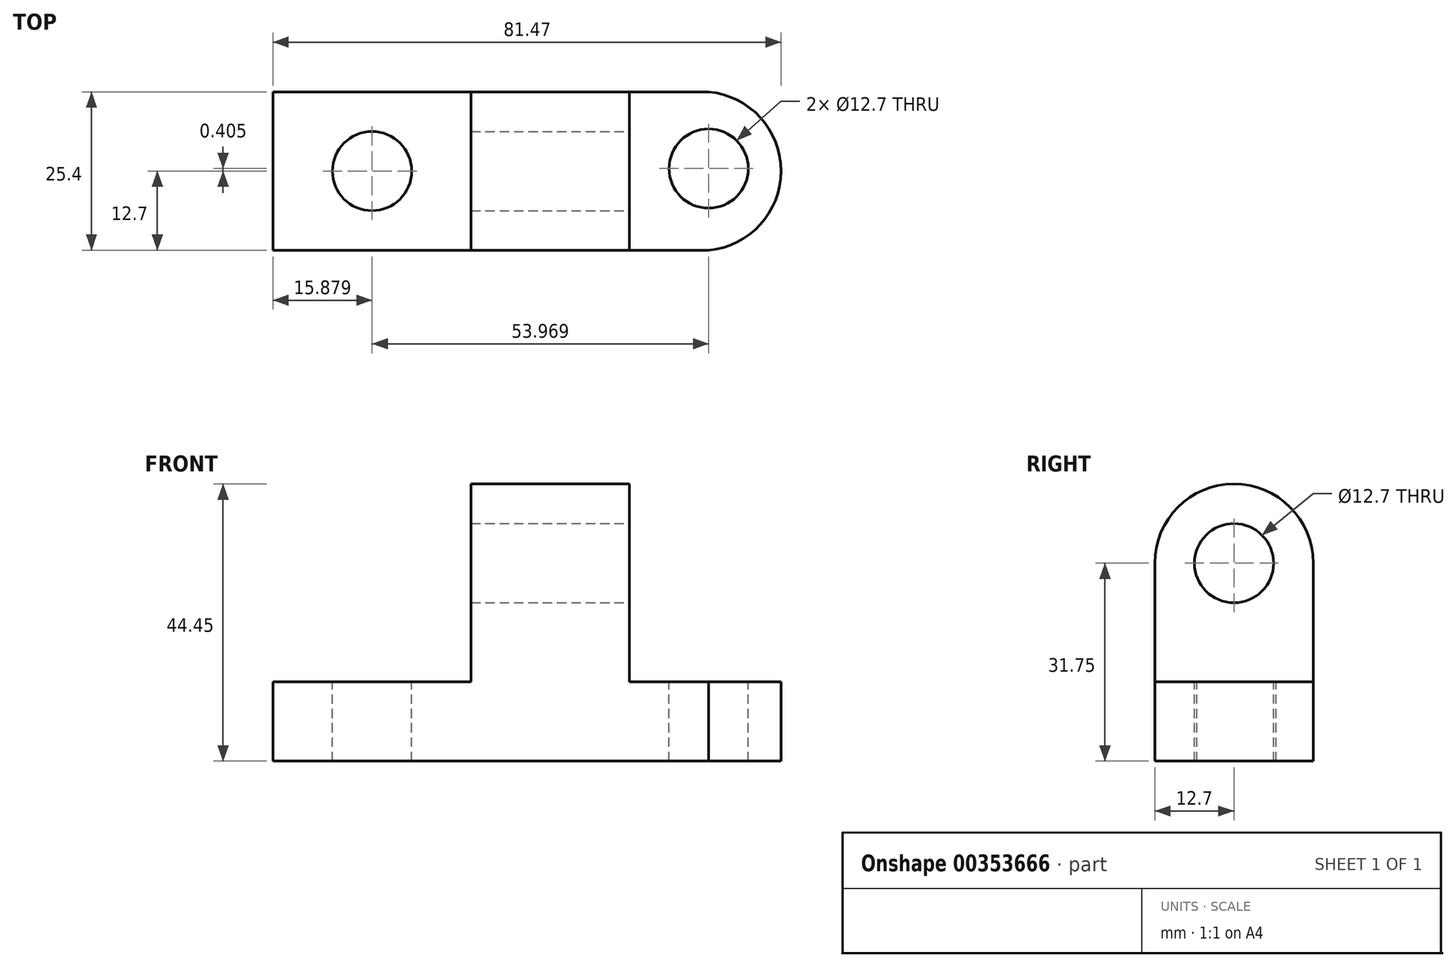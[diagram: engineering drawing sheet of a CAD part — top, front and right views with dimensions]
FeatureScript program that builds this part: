
annotation { "Feature Type Name" : "Feature", "Feature Type Description" : "" }
export const myFeature = defineFeature(function(context is Context, id is Id, definition is map)
    precondition{}
    {
        {
            var Q0;
            Q0=qCreatedBy(makeId("Front.planeOp"),FACE);
            var sketch = newSketch(context, id + "F0", { "sketchPlane" : qUnion([Q0])});
            skLineSegment(sketch, "E0", {"start": v(-42.78, 63.5) * mm, "end": v(-42.78, 0) * mm});
            skLineSegment(sketch, "E1", {"start": v(-42.78, 0) * mm, "end": v(46.12, 0) * mm});
            skLineSegment(sketch, "E2", {"start": v(46.12, 0) * mm, "end": v(46.12, 63.5) * mm});
            skLineSegment(sketch, "E3", {"start": v(46.12, 63.5) * mm, "end": v(-42.78, 63.5) * mm});
            skSolve(sketch);
        }
        {
            var Q0;
            Q0 = qSketchRegion(id + "F0", true);
            extrude(context, id + "F1", {"entities" : qUnion([Q0]), "depth" : 25.4 * mm});
        }
        {
            var Q0;
            Q0=makeQuery(id+"F1.opExtrude","CAP_FACE",FACE,{"disambiguationData":[OSD([sQuery(id+"F0.wireOp",EDGE,"E0"),sQuery(id+"F0.wireOp",EDGE,"E1"),sQuery(id+"F0.wireOp",EDGE,"E2"),sQuery(id+"F0.wireOp",EDGE,"E3")])],"isStart":false});
            var sketch = newSketch(context, id + "F2", { "sketchPlane" : qUnion([Q0])});
            skLineSegment(sketch, "E4", {"start": v(14.37, 63.5) * mm, "end": v(14.37, 12.7) * mm});
            skLineSegment(sketch, "E5", {"start": v(14.37, 12.7) * mm, "end": v(46.12, 12.7) * mm});
            skLineSegment(sketch, "E6", {"start": v(-11.03, 63.5) * mm, "end": v(-11.03, 12.7) * mm});
            skLineSegment(sketch, "E7", {"start": v(-11.03, 12.7) * mm, "end": v(-42.78, 12.7) * mm});
            skSolve(sketch);
        }
        {
            var Q0;
            Q0 = qSketchRegion(id + "F2", true);
            var Q1;
            {var subQ0=sQuery(id+"F2.wireOp",EDGE,"E6");Q1=makeQuery(id+"F2.imprint","IMPRINT",FACE,{"disambiguationData":[TD([[makeQuery(id+"F2.imprint","IMPRINT",EDGE,{"derivedFrom":subQ0}),-1.0]])]});}
            var Q2;
            {var subQ0=sQuery(id+"F2.wireOp",EDGE,"E4");Q2=makeQuery(id+"F2.imprint","IMPRINT",FACE,{"disambiguationData":[TD([[makeQuery(id+"F2.imprint","IMPRINT",EDGE,{"derivedFrom":subQ0}),1.0]])]});}
            extrude(context, id + "F3", {"entities" : qUnion([Q0, Q1, Q2]), "operationType" : NewBodyOperationType.REMOVE, "oppositeDirection" : true, "depth" : 25.4 * mm});
        }
        {
            var Q0;
            Q0=makeQuery(id+"F3.boolean.opBoolean","COPY",FACE,{"derivedFrom":makeQuery(id+"F3.opExtrude","SWEPT_FACE",FACE,{"disambiguationData":[OSD([sQuery(id+"F2.wireOp",EDGE,"E4")])]})});
            var sketch = newSketch(context, id + "F4", { "sketchPlane" : qUnion([Q0])});
            skCircle(sketch, "E8", {"center": v(-12.7, 31.75) * mm, "radius": 6.35 * mm});
            skArc(sketch, "E9", {"start": v(0, 31.75) * mm, "mid": v(-12.7, 44.45) * mm, "end": v(-25.4, 31.75) * mm});
            skPoint(sketch, "E9.startSnap0", {"position": v(0, 38.1) * mm});
            skSolve(sketch);
        }
        {
            var Q0;
            {var subQ0=sQuery(id+"F4.wireOp",EDGE,"E9");Q0=makeQuery(id+"F4.imprint","IMPRINT",FACE,{"disambiguationData":[TD([[makeQuery(id+"F4.imprint","IMPRINT",EDGE,{"derivedFrom":subQ0}),-1.0]])]});}
            var Q1;
            Q1=makeQuery(id+"F4.imprint","IMPRINT",FACE,{"disambiguationData":[TD([[makeQuery(id+"F4.imprint","IMPRINT",EDGE,{"derivedFrom":sQuery(id+"F4.wireOp",EDGE,"E8")}),1.0]])]});
            extrude(context, id + "F5", {"entities" : qUnion([Q0, Q1]), "operationType" : NewBodyOperationType.REMOVE, "oppositeDirection" : true, "depth" : 25.4 * mm});
        }
        {
            var Q0;
            Q0=makeQuery(id+"F3.boolean.opBoolean","COPY",FACE,{"derivedFrom":makeQuery(id+"F3.opExtrude","SWEPT_FACE",FACE,{"disambiguationData":[OSD([sQuery(id+"F2.wireOp",EDGE,"E5")])]})});
            var sketch = newSketch(context, id + "F6", { "sketchPlane" : qUnion([Q0])});
            skCircle(sketch, "E10", {"center": v(27.07, -12.3) * mm, "radius": 6.35 * mm});
            skArc(sketch, "E11", {"start": v(27.07, -25.4) * mm, "mid": v(38.7, -12.7) * mm, "end": v(27.07, 0) * mm});
            skPoint(sketch, "E11.startSnap0", {"position": v(30.25, -25.4) * mm});
            skSolve(sketch);
        }
        {
            var Q0;
            Q0 = qSketchRegion(id + "F6", true);
            var Q1;
            {var subQ0=sQuery(id+"F6.wireOp",EDGE,"E11");Q1=makeQuery(id+"F6.imprint","IMPRINT",FACE,{"disambiguationData":[TD([[makeQuery(id+"F6.imprint","IMPRINT",EDGE,{"derivedFrom":subQ0}),-1.0]])]});}
            extrude(context, id + "F7", {"entities" : qUnion([Q0, Q1]), "operationType" : NewBodyOperationType.REMOVE, "oppositeDirection" : true, "depth" : 25.4 * mm});
        }
        {
            var Q0;
            Q0=makeQuery(id+"F3.boolean.opBoolean","COPY",FACE,{"derivedFrom":makeQuery(id+"F3.opExtrude","SWEPT_FACE",FACE,{"disambiguationData":[OSD([sQuery(id+"F2.wireOp",EDGE,"E7")])]})});
            var sketch = newSketch(context, id + "F8", { "sketchPlane" : qUnion([Q0])});
            skCircle(sketch, "E12", {"center": v(-26.9, -12.7) * mm, "radius": 6.35 * mm});
            skArc(sketch, "E13", {"start": v(-26.9, 0) * mm, "mid": v(-39.96, -12.7) * mm, "end": v(-26.9, -25.4) * mm});
            skSolve(sketch);
        }
        {
            var Q0;
            Q0 = qSketchRegion(id + "F8", true);
            var Q1;
            {var subQ1=sQuery(id+"F2.wireOp",EDGE,"E7");var subQ6=makeQuery(id+"F3.boolean.opBoolean","COPY",EDGE,{"derivedFrom":makeQuery(id+"F3.opExtrude","SWEPT_EDGE",EDGE,{"disambiguationData":[OSD([sQuery(id+"F0.wireOp",EDGE,"E0"),subQ1])]})});Q1=makeQuery(id+"F8.imprint","IMPRINT",FACE,{"disambiguationData":[TD([[makeQuery(id+"F8.imprint","IMPRINT",EDGE,{"derivedFrom":subQ6}),1.0]])]});}
            extrude(context, id + "F9", {"entities" : qUnion([Q0, Q1]), "operationType" : NewBodyOperationType.REMOVE, "oppositeDirection" : true, "depth" : 25.4 * mm});
        }
    });
